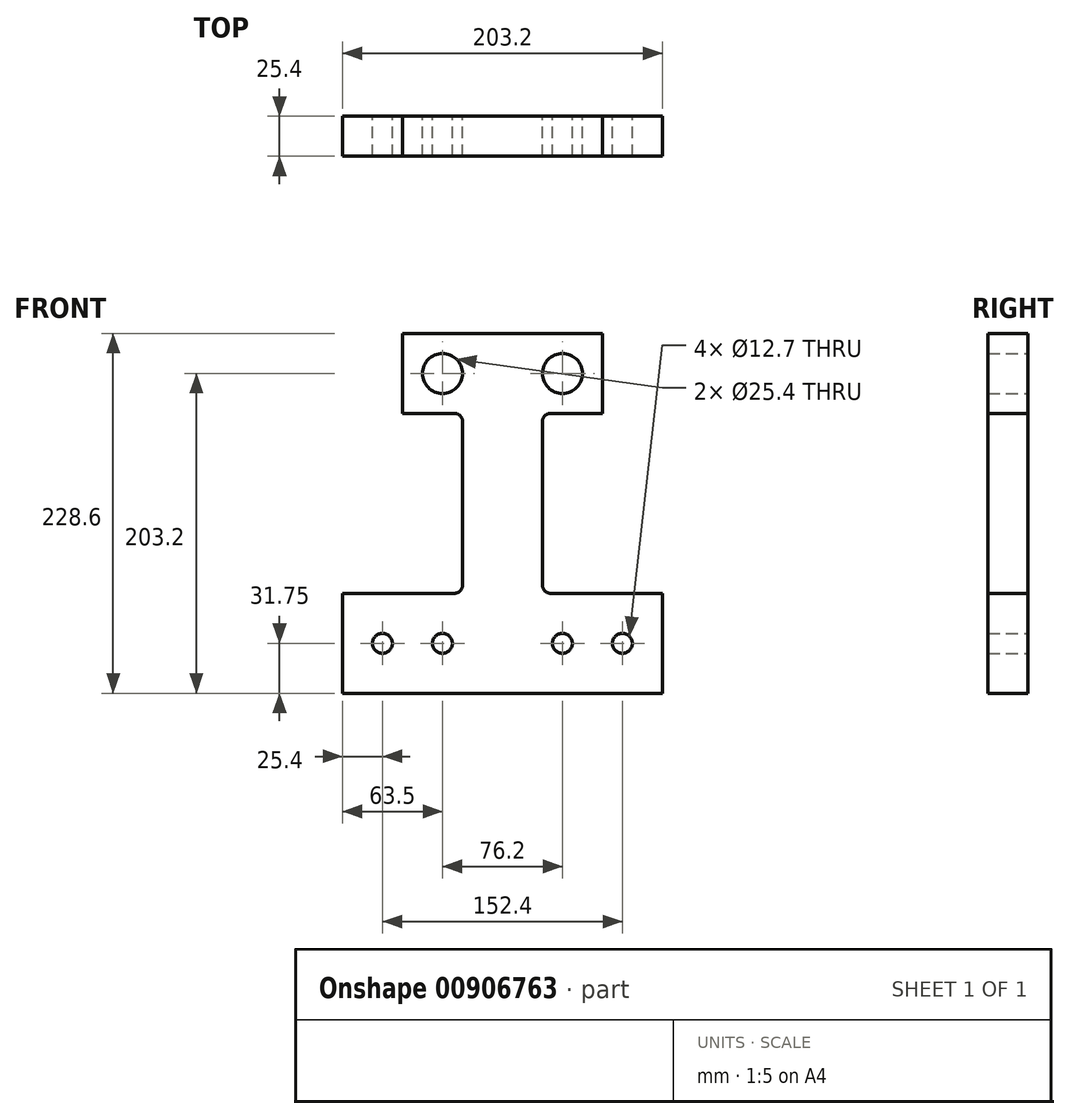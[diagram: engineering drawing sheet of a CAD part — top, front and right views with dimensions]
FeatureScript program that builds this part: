
annotation { "Feature Type Name" : "Feature", "Feature Type Description" : "" }
export const myFeature = defineFeature(function(context is Context, id is Id, definition is map)
    precondition{}
    {
        {
            var Q0;
            Q0=qCreatedBy(makeId("Front.planeOp"),FACE);
            var sketch = newSketch(context, id + "F0", { "sketchPlane" : qUnion([Q0])});
            skLineSegment(sketch, "E0", {"start": v(0, 0) * mm, "end": v(25.4, 0) * mm});
            skLineSegment(sketch, "E1", {"start": v(25.4, 0) * mm, "end": v(25.4, 76.2) * mm});
            skLineSegment(sketch, "E2", {"start": v(25.4, 76.2) * mm, "end": v(63.5, 76.2) * mm});
            skLineSegment(sketch, "E3", {"start": v(63.5, 76.2) * mm, "end": v(63.5, 127) * mm});
            skLineSegment(sketch, "E4", {"start": v(63.5, 127) * mm, "end": v(-63.5, 127) * mm});
            skLineSegment(sketch, "E5", {"start": v(-63.5, 127) * mm, "end": v(-63.5, 76.2) * mm});
            skLineSegment(sketch, "E6", {"start": v(-63.5, 76.2) * mm, "end": v(-25.4, 76.2) * mm});
            skLineSegment(sketch, "E7", {"start": v(-25.4, 76.2) * mm, "end": v(-25.4, 0) * mm});
            skLineSegment(sketch, "E8", {"start": v(-25.4, 0) * mm, "end": v(0, 0) * mm});
            skLineSegment(sketch, "E9", {"start": v(-25.4, 0) * mm, "end": v(-25.4, -38.1) * mm});
            skLineSegment(sketch, "E10", {"start": v(-25.4, -38.1) * mm, "end": v(-101.6, -38.1) * mm});
            skLineSegment(sketch, "E11", {"start": v(-101.6, -38.1) * mm, "end": v(-101.6, -101.6) * mm});
            skLineSegment(sketch, "E12", {"start": v(-101.6, -101.6) * mm, "end": v(101.6, -101.6) * mm});
            skLineSegment(sketch, "E13", {"start": v(101.6, -101.6) * mm, "end": v(101.6, -38.1) * mm});
            skLineSegment(sketch, "E14", {"start": v(101.6, -38.1) * mm, "end": v(25.4, -38.1) * mm});
            skLineSegment(sketch, "E15", {"start": v(25.4, -38.1) * mm, "end": v(25.4, 0) * mm});
            skCircle(sketch, "E16", {"center": v(-76.2, -69.85) * mm, "radius": 6.35 * mm});
            skCircle(sketch, "E17", {"center": v(-38.1, -69.85) * mm, "radius": 6.35 * mm});
            skCircle(sketch, "E18.MirrorC", {"center": v(76.2, -69.85) * mm, "radius": 6.35 * mm});
            skCircle(sketch, "E19.MirrorC", {"center": v(38.1, -69.85) * mm, "radius": 6.35 * mm});
            skCircle(sketch, "E20", {"center": v(-38.1, 101.6) * mm, "radius": 12.7 * mm});
            skCircle(sketch, "E21", {"center": v(38.1, 101.6) * mm, "radius": 12.7 * mm});
            skSolve(sketch);
        }
        {
            var Q0;
            Q0 = qSketchRegion(id + "F0", true);
            extrude(context, id + "F1", {"entities" : qUnion([Q0]), "depth" : 25.4 * mm, "offsetDistance" : 25.4 * mm});
        }
        {
            var Q0;
            Q0=makeQuery(id+"F1.opExtrude","SWEPT_EDGE",EDGE,{"disambiguationData":[OSD([sQuery(id+"F0.wireOp",EDGE,"E6"),sQuery(id+"F0.wireOp",EDGE,"E7")])]});
            var Q1;
            Q1=makeQuery(id+"F1.opExtrude","SWEPT_EDGE",EDGE,{"disambiguationData":[OSD([sQuery(id+"F0.wireOp",EDGE,"E9"),sQuery(id+"F0.wireOp",EDGE,"E10")])]});
            var Q2;
            Q2=makeQuery(id+"F1.opExtrude","SWEPT_EDGE",EDGE,{"disambiguationData":[OSD([sQuery(id+"F0.wireOp",EDGE,"E14"),sQuery(id+"F0.wireOp",EDGE,"E15")])]});
            var Q3;
            Q3=makeQuery(id+"F1.opExtrude","SWEPT_EDGE",EDGE,{"disambiguationData":[OSD([sQuery(id+"F0.wireOp",EDGE,"E1"),sQuery(id+"F0.wireOp",EDGE,"E2")])]});
            fillet(context, id + "F2", {"entities" : qUnion([Q0, Q1, Q2, Q3]), "radius" : 5.08 * mm, "tangentPropagation" : true, "allowEdgeOverflow" : false});
        }
    });
